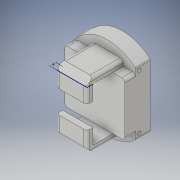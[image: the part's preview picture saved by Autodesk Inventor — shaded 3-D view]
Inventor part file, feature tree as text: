
AUTODESK INVENTOR PART (.ipt)
format: ipt  version: 2019 (Build 230136000, 136)  size: 206,848 bytes
history: native  units: mm
features: sketch x8, extrude x7, other x2, fillet x2, loft x1, mirror x1
ambient origin geometry x8: Origin, YZ Plane, XZ Plane, XY Plane, X Axis, Y Axis, Z Axis, Center Point
bodies: Body1 (feature_tree), Body2 (feature_tree)
feature tree (21):
  other  "Bryła1"
  sketch  "Szkic1"
  extrude  "Wyciągnięcie proste1"  Depth=55.0mm
  extrude  "Wyciągnięcie proste2"  Depth=10.0mm TaperAngle=0.0deg
  extrude  "Wyciągnięcie proste3"  Depth=5.0mm
  extrude  "Wyciągnięcie proste4"  Depth=3.0mm
  extrude  "Wyciągnięcie proste5"  Depth=8.0mm TaperAngle=0.0deg
  extrude  "Wyciągnięcie proste6"  Depth=10.0mm TaperAngle=0.0deg
  sketch  "Szkic9"
  loft  "Wyciągnięcie złożone1"
  extrude  "Wyciągnięcie proste7"  Depth=7.0mm TaperAngle=0.0deg
  mirror  "Odbij1"
  fillet  "Zaokrąglenie1"  Radius=2.5mm
  fillet  "Zaokrąglenie2"  Radius=2.5mm
  sketch  "Szkic2"
  sketch  "Szkic3"
  sketch  "Szkic4"
  sketch  "Szkic5"
  sketch  "Szkic6"
  sketch  "Szkic7"
  other  "Krawędzie1"
